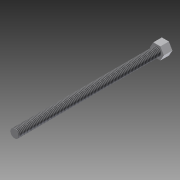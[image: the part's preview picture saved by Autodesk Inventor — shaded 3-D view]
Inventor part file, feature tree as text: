
AUTODESK INVENTOR PART (.ipt)
format: ipt  version: 2014 (Build 180170000, 170)  size: 85,504 bytes
history: native  units: mm
features: extrude x2, sketch x2, thread x1
ambient origin geometry x8: Origin, YZ Plane, XZ Plane, XY Plane, X Axis, Y Axis, Z Axis, Center Point
bodies: Solid1 (feature_tree)
feature tree (5):
  extrude  "Extrusion1"  Depth=50.0mm TaperAngle=0.0deg
  extrude  "Extrusion2"  Depth=10.0mm TaperAngle=0.0deg
  thread  "Thread1"  [1 undecoded]
  sketch  "Sketch1"  dims[d0=3.0mm d1=50.0mm d2=0.0mm]
  sketch  "Sketch2"  dims[d3=3.0mm d4=0.0mm d5=10.0mm d6=0.0mm]
note: 1 required parameter value undecoded (feature->parameter linkage not recoverable at this tier; creation-order binding heuristic only, values carry confidence <= 0.55)
